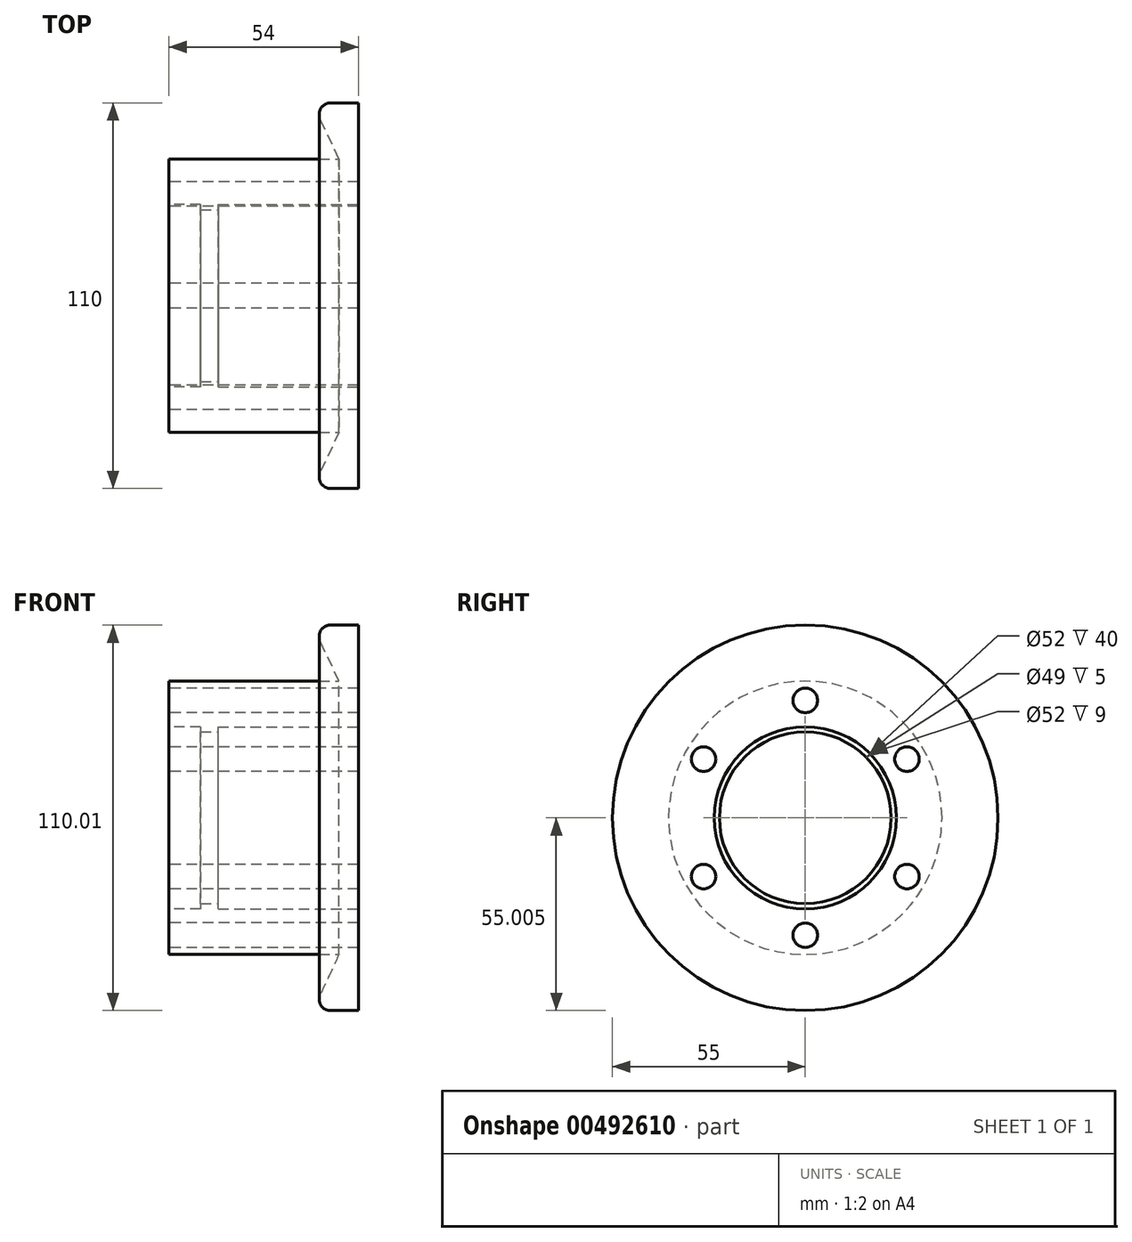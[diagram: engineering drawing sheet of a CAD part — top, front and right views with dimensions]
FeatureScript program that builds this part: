
annotation { "Feature Type Name" : "Feature", "Feature Type Description" : "" }
export const myFeature = defineFeature(function(context is Context, id is Id, definition is map)
    precondition{}
    {
        {
            var Q0;
            Q0=qCreatedBy(makeId("Front.planeOp"),FACE);
            var sketch = newSketch(context, id + "F0", { "sketchPlane" : qUnion([Q0])});
            skLineSegment(sketch, "E0", {"start": v(22.98, 53.18) * mm, "end": v(31, 53.18) * mm});
            skLineSegment(sketch, "E1", {"start": v(20.1, 48.66) * mm, "end": v(25.46, 37.18) * mm});
            skLineSegment(sketch, "E2", {"start": v(31, 53.18) * mm, "end": v(31, 37.18) * mm});
            skLineSegment(sketch, "E3", {"start": v(25.46, 37.18) * mm, "end": v(-23, 37.18) * mm});
            skArc(sketch, "E4.filletArc", {"start": v(22.98, 53.18) * mm, "mid": v(20.3, 51.7) * mm, "end": v(20.1, 48.66) * mm});
            skLineSegment(sketch, "E5", {"start": v(31, 37.18) * mm, "end": v(31, -1.83) * mm});
            skLineSegment(sketch, "E6", {"start": v(31, -1.83) * mm, "end": v(-23, -1.83) * mm});
            skLineSegment(sketch, "E7", {"start": v(-23, -1.83) * mm, "end": v(-23, 37.17) * mm});
            skSolve(sketch);
        }
        {
            var Q0;
            Q0=makeQuery(id+"F0.imprint","IMPRINT",FACE,{"disambiguationData":[TD([[makeQuery(id+"F0.imprint","IMPRINT",EDGE,{"derivedFrom":sQuery(id+"F0.wireOp",EDGE,"E0")}),-1.0]])]});
            var Q1;
            Q1=sQuery(id+"F0.wireOp",EDGE,"E6");
            revolve(context, id + "F1", {"entities" : qUnion([Q0]), "axis" : qUnion([Q1]), "revolveType" : RevolveType.FULL});
        }
        {
            var Q0;
            Q0=makeQuery(id+"F1.opRevolve","SWEPT_FACE",FACE,{"disambiguationData":[OSD([sQuery(id+"F0.wireOp",EDGE,"E2"),sQuery(id+"F0.wireOp",EDGE,"E5")])]});
            var sketch = newSketch(context, id + "F2", { "sketchPlane" : qUnion([Q0])});
            skCircle(sketch, "E8", {"center": v(0, -1.83) * mm, "radius": 26 * mm});
            skSolve(sketch);
        }
        {
            var Q0;
            Q0=makeQuery(id+"F2.imprint","IMPRINT",FACE,{"disambiguationData":[TD([[makeQuery(id+"F2.imprint","IMPRINT",EDGE,{"derivedFrom":sQuery(id+"F2.wireOp",EDGE,"E8")}),1.0]])]});
            extrude(context, id + "F3", {"entities" : qUnion([Q0]), "operationType" : NewBodyOperationType.REMOVE, "oppositeDirection" : true, "depth" : 40 * mm});
        }
        {
            var Q0;
            Q0=makeQuery(id+"F3.boolean.opBoolean","COPY",FACE,{"derivedFrom":makeQuery(id+"F3.opExtrude","CAP_FACE",FACE,{"disambiguationData":[OSD([sQuery(id+"F2.wireOp",EDGE,"E8")])],"isStart":false})});
            var sketch = newSketch(context, id + "F4", { "sketchPlane" : qUnion([Q0])});
            skCircle(sketch, "E9", {"center": v(0, -1.83) * mm, "radius": 24.5 * mm});
            skSolve(sketch);
        }
        {
            var Q0;
            Q0=makeQuery(id+"F4.imprint","IMPRINT",FACE,{"disambiguationData":[TD([[makeQuery(id+"F4.imprint","IMPRINT",EDGE,{"derivedFrom":sQuery(id+"F4.wireOp",EDGE,"E9")}),1.0]])]});
            extrude(context, id + "F5", {"entities" : qUnion([Q0]), "operationType" : NewBodyOperationType.REMOVE, "oppositeDirection" : true, "depth" : 5 * mm});
        }
        {
            var Q0;
            Q0=makeQuery(id+"F1.opRevolve","SWEPT_FACE",FACE,{"disambiguationData":[OSD([sQuery(id+"F0.wireOp",EDGE,"E7")])]});
            var sketch = newSketch(context, id + "F6", { "sketchPlane" : qUnion([Q0])});
            skCircle(sketch, "E10", {"center": v(0, -1.83) * mm, "radius": 26 * mm});
            skSolve(sketch);
        }
        {
            var Q0;
            Q0=makeQuery(id+"F6.imprint","IMPRINT",FACE,{"disambiguationData":[TD([[makeQuery(id+"F6.imprint","IMPRINT",EDGE,{"derivedFrom":sQuery(id+"F6.wireOp",EDGE,"E10")}),1.0]])]});
            extrude(context, id + "F7", {"entities" : qUnion([Q0]), "operationType" : NewBodyOperationType.REMOVE, "oppositeDirection" : true, "depth" : 9 * mm});
        }
        {
            var Q0;
            Q0=makeQuery(id+"F1.opRevolve","SWEPT_FACE",FACE,{"disambiguationData":[OSD([sQuery(id+"F0.wireOp",EDGE,"E7")])]});
            var sketch = newSketch(context, id + "F8", { "sketchPlane" : qUnion([Q0])});
            skCircle(sketch, "E11", {"center": v(0, 31.67) * mm, "radius": 3.5 * mm});
            skCircle(sketch, "E12.1.0", {"center": v(-29.01, 14.92) * mm, "radius": 3.5 * mm});
            skCircle(sketch, "E12.2.0", {"center": v(-29.01, -18.58) * mm, "radius": 3.5 * mm});
            skCircle(sketch, "E12.3.0", {"center": v(0, -35.33) * mm, "radius": 3.5 * mm});
            skCircle(sketch, "E12.4.0", {"center": v(29.01, -18.58) * mm, "radius": 3.5 * mm});
            skCircle(sketch, "E12.5.0", {"center": v(29.01, 14.92) * mm, "radius": 3.5 * mm});
            skPoint(sketch, "E12.center", {"position": v(0, -1.83) * mm});
            skLineSegment(sketch, "E13", {"start": v(0, 31.67) * mm, "end": v(0, 24.17) * mm});
            skLineSegment(sketch, "E14", {"start": v(0, 24.17) * mm, "end": v(0, 37.17) * mm});
            skSolve(sketch);
        }
        {
            var Q0;
            Q0=makeQuery(id+"F8.imprint","IMPRINT",FACE,{"disambiguationData":[TD([[makeQuery(id+"F8.imprint","IMPRINT",EDGE,{"derivedFrom":sQuery(id+"F8.wireOp",EDGE,"E12.1.0")}),1.0]])]});
            var Q1;
            Q1=makeQuery(id+"F8.imprint","IMPRINT",FACE,{"disambiguationData":[TD([[makeQuery(id+"F8.imprint","IMPRINT",EDGE,{"derivedFrom":sQuery(id+"F8.wireOp",EDGE,"E12.2.0")}),1.0]])]});
            var Q2;
            Q2=makeQuery(id+"F8.imprint","IMPRINT",FACE,{"disambiguationData":[TD([[makeQuery(id+"F8.imprint","IMPRINT",EDGE,{"derivedFrom":sQuery(id+"F8.wireOp",EDGE,"E12.3.0")}),1.0]])]});
            var Q3;
            Q3=makeQuery(id+"F8.imprint","IMPRINT",FACE,{"disambiguationData":[TD([[makeQuery(id+"F8.imprint","IMPRINT",EDGE,{"derivedFrom":sQuery(id+"F8.wireOp",EDGE,"E12.4.0")}),1.0]])]});
            var Q4;
            Q4=makeQuery(id+"F8.imprint","IMPRINT",FACE,{"disambiguationData":[TD([[makeQuery(id+"F8.imprint","IMPRINT",EDGE,{"derivedFrom":sQuery(id+"F8.wireOp",EDGE,"E12.5.0")}),1.0]])]});
            var Q5;
            Q5=makeQuery(id+"F8.imprint","IMPRINT",FACE,{"disambiguationData":[TD([[makeQuery(id+"F8.imprint","IMPRINT",EDGE,{"derivedFrom":sQuery(id+"F8.wireOp",EDGE,"E11")}),1.0]])]});
            extrude(context, id + "F9", {"entities" : qUnion([Q0, Q1, Q2, Q3, Q4, Q5]), "operationType" : NewBodyOperationType.REMOVE, "endBound" : BoundingType.THROUGH_ALL, "oppositeDirection" : true, "depth" : 25 * mm});
        }
    });
